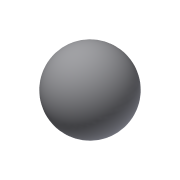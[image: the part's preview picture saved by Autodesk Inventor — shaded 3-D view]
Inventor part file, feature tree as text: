
AUTODESK INVENTOR PART (.ipt)
format: ipt  version: 2014 (Build 180170000, 170)  size: 98,816 bytes
history: native  units: mm
features: revolve x1, sketch x1
ambient origin geometry x8: Origin, YZ Plane, XZ Plane, XY Plane, X Axis, Y Axis, Z Axis, Center Point
bodies: Volumenkörper1 (feature_tree)
feature tree (2):
  revolve  "Umdrehung1"
  sketch  "Skizze1"  dims[d0=9.525mm d1=90.0deg]
